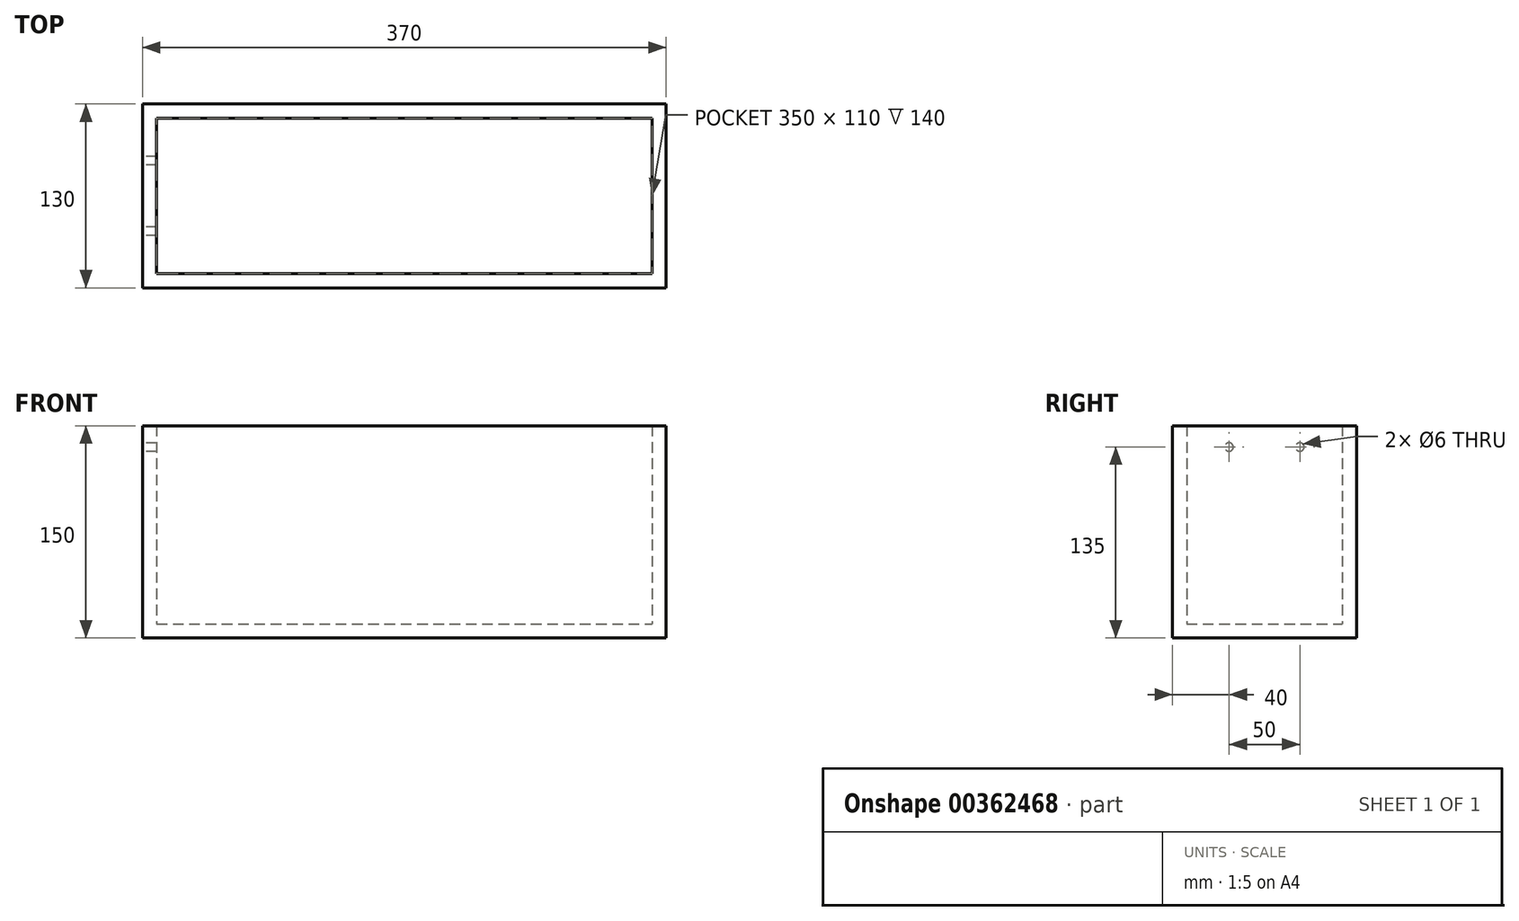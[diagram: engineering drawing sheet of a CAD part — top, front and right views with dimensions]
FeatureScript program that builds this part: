
annotation { "Feature Type Name" : "Feature", "Feature Type Description" : "" }
export const myFeature = defineFeature(function(context is Context, id is Id, definition is map)
    precondition{}
    {
        {
            var Q0;
            Q0=qCreatedBy(makeId("Top.planeOp"),FACE);
            var sketch = newSketch(context, id + "F0", { "sketchPlane" : qUnion([Q0])});
            skLineSegment(sketch, "E0.bottom", {"start": v(-185, -65) * mm, "end": v(185, -65) * mm});
            skLineSegment(sketch, "E0.top", {"start": v(-185, 65) * mm, "end": v(185, 65) * mm});
            skLineSegment(sketch, "E0.left", {"start": v(-185, -65) * mm, "end": v(-185, 65) * mm});
            skLineSegment(sketch, "E0.right", {"start": v(185, -65) * mm, "end": v(185, 65) * mm});
            skPoint(sketch, "E0.middle", {"position": v(0, 0) * mm});
            skSolve(sketch);
        }
        {
            var Q0;
            Q0 = qSketchRegion(id + "F0", true);
            extrude(context, id + "F1", {"entities" : qUnion([Q0]), "depth" : 150 * mm, "offsetDistance" : 25 * mm});
        }
        {
            var Q0;
            Q0=makeQuery(id+"F1.opExtrude","CAP_FACE",FACE,{"disambiguationData":[OSD([sQuery(id+"F0.wireOp",EDGE,"E0.bottom"),sQuery(id+"F0.wireOp",EDGE,"E0.top"),sQuery(id+"F0.wireOp",EDGE,"E0.left"),sQuery(id+"F0.wireOp",EDGE,"E0.right")])],"isStart":false});
            shell(context, id + "F2", {"entities" : qUnion([Q0]), "thickness" : 10 * mm});
        }
        {
            var Q0;
            Q0=makeQuery(id+"F1.opExtrude","SWEPT_FACE",FACE,{"disambiguationData":[OSD([sQuery(id+"F0.wireOp",EDGE,"E0.left")])]});
            var sketch = newSketch(context, id + "F3", { "sketchPlane" : qUnion([Q0])});
            skLineSegment(sketch, "E1", {"start": v(0, 150) * mm, "end": v(0, 0) * mm, "construction": true});
            skCircle(sketch, "E2", {"center": v(-25, 135) * mm, "radius": 3 * mm});
            skCircle(sketch, "E3.MirrorC", {"center": v(25, 135) * mm, "radius": 3 * mm});
            skSolve(sketch);
        }
        {
            var Q0;
            Q0 = qSketchRegion(id + "F3", true);
            extrude(context, id + "F4", {"entities" : qUnion([Q0]), "operationType" : NewBodyOperationType.REMOVE, "oppositeDirection" : true, "depth" : 25 * mm, "offsetDistance" : 25 * mm});
        }
    });
